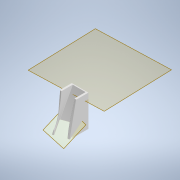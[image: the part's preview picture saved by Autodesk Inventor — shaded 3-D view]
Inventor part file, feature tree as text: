
AUTODESK INVENTOR PART (.ipt)
format: ipt  version: 2022 (Build 260153000, 153)  size: 364,032 bytes
history: native  units: mm
features: other x9, reference x9, sketch x8, extrude x4, fillet x4, loft x2, projected_geometry x2
ambient origin geometry x8: Origin, YZ Plane, XZ Plane, XY Plane, X Axis, Y Axis, Z Axis, Center Point
bodies: Body1 (feature_tree)
feature tree (38):
  other  "Твердое тело1"
  other  "РабТочка1"
  extrude  "Выдавливание1"  Depth=2.0mm
  sketch  "Эскиз2"
  other  "РабПлоскость2"
  loft  "Лофт1"
  extrude  "Выдавливание2"  Depth=26.0mm TaperAngle=0.0deg
  loft  "Лофт2"
  fillet  "Сопряжение1"  Radius=2.0mm
  extrude  "Выдавливание3"  Depth=2.0mm
  fillet  "Сопряжение2"  [1 undecoded]
  fillet  "Сопряжение3"  [1 undecoded]
  other  "РабПлоскость3"
  extrude  "Выдавливание4"  Depth=1.5mm
  fillet  "Сопряжение4"  Radius=20.0mm
  sketch  "Эскиз1"
  reference  "Ссылка1"
  reference  "Ссылка2"
  projected_geometry  "Спроецированная петля1"
  sketch  "Эскиз3"
  reference  "Ссылка3"
  sketch  "Эскиз4"
  reference  "Ссылка4"
  sketch  "Эскиз5"
  projected_geometry  "Спроецированная петля2"
  reference  "Ссылка5"
  sketch  "Эскиз6"
  reference  "Ссылка6"
  reference  "Ссылка7"
  sketch  "Эскиз7"
  reference  "Ссылка8"
  sketch  "Эскиз8"
  reference  "Ссылка9"
  other  "<userpath>\Documents\Git\MZCAT_2024\MZCAT.iam"
  other  "MZCAT.iam"
  other  "CAT_protector:1"
  other  "vydacha_backstenka:1"
  other  "CAT_wheel:3"
note: 2 required parameter values undecoded (feature->parameter linkage not recoverable at this tier; creation-order binding heuristic only, values carry confidence <= 0.55)
